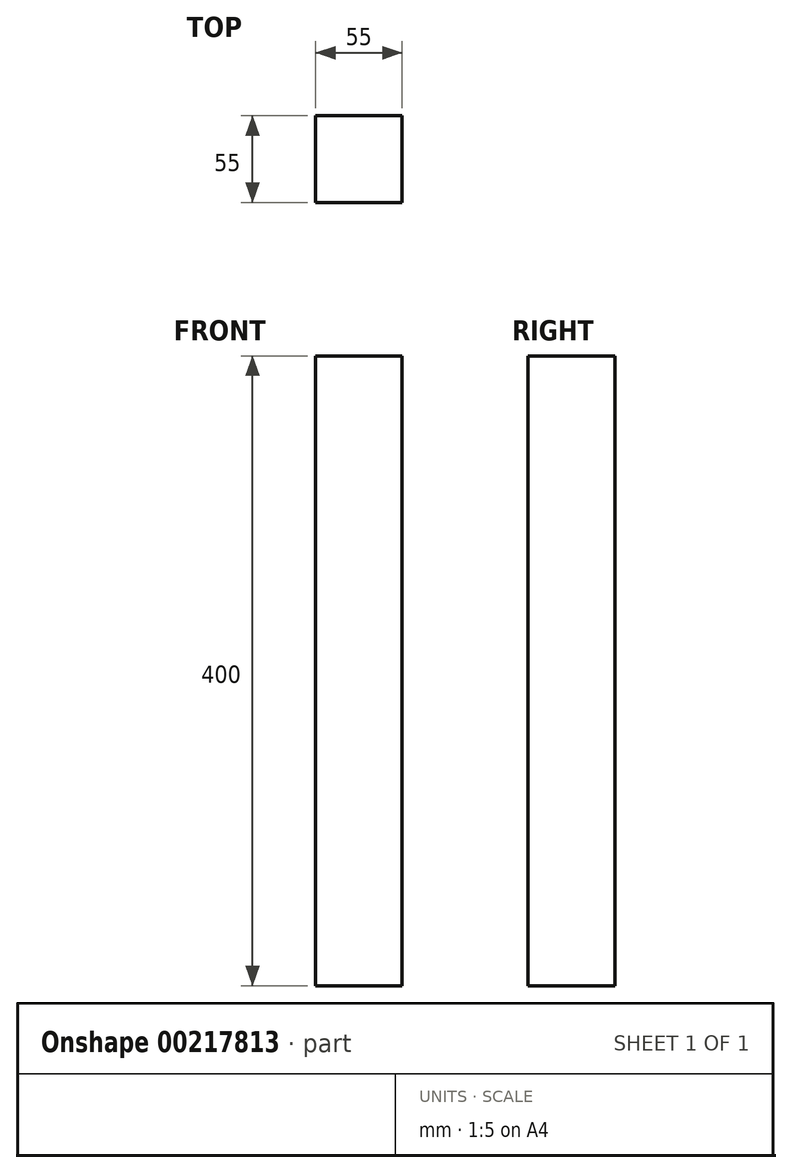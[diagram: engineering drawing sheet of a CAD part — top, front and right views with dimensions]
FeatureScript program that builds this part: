
annotation { "Feature Type Name" : "Feature", "Feature Type Description" : "" }
export const myFeature = defineFeature(function(context is Context, id is Id, definition is map)
    precondition{}
    {
        {
            var Q0;
            Q0=qCreatedBy(makeId("Front.planeOp"),FACE);
            var sketch = newSketch(context, id + "F0", { "sketchPlane" : qUnion([Q0])});
            skLineSegment(sketch, "E0.bottom", {"start": v(0, 0) * mm, "end": v(-55, 0) * mm});
            skLineSegment(sketch, "E0.top", {"start": v(0, 400) * mm, "end": v(-55, 400) * mm});
            skLineSegment(sketch, "E0.left", {"start": v(0, 0) * mm, "end": v(0, 400) * mm});
            skLineSegment(sketch, "E0.right", {"start": v(-55, 0) * mm, "end": v(-55, 400) * mm});
            skSolve(sketch);
        }
        {
            var Q0;
            Q0 = qSketchRegion(id + "F0", true);
            extrude(context, id + "F1", {"entities" : qUnion([Q0]), "depth" : 55 * mm});
        }
    });
